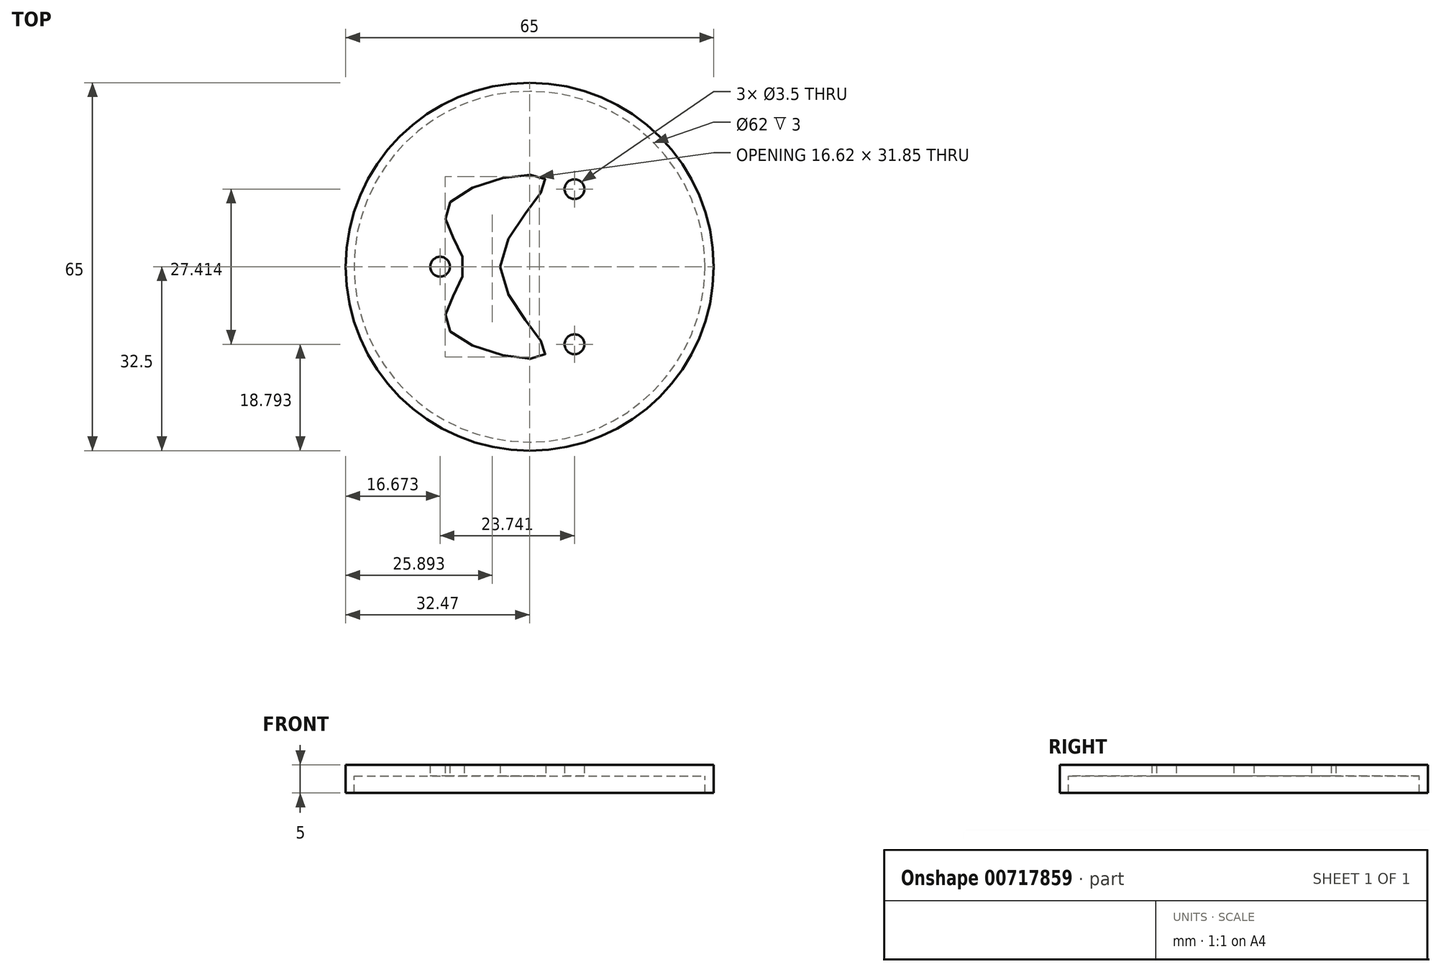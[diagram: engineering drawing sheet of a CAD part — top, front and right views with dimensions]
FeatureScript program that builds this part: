
annotation { "Feature Type Name" : "Feature", "Feature Type Description" : "" }
export const myFeature = defineFeature(function(context is Context, id is Id, definition is map)
    precondition{}
    {
        {
            var Q0;
            Q0=qCreatedBy(makeId("Top.planeOp"),FACE);
            var sketch = newSketch(context, id + "F0", { "sketchPlane" : qUnion([Q0])});
            skCircle(sketch, "E0", {"center": v(0.03, 0) * mm, "radius": 32.5 * mm});
            skCircle(sketch, "E1", {"center": v(-15.8, 0) * mm, "radius": 1.75 * mm});
            skCircle(sketch, "E2.1.0", {"center": v(7.94, -13.7) * mm, "radius": 1.75 * mm});
            skCircle(sketch, "E2.2.0", {"center": v(7.94, 13.7) * mm, "radius": 1.75 * mm});
            skPoint(sketch, "E3", {"position": v(2.67, 15.6) * mm});
            skPoint(sketch, "E4.MirrorP", {"position": v(2.67, -15.6) * mm});
            skPoint(sketch, "E5", {"position": v(-5.16, 0) * mm});
            skPoint(sketch, "E6", {"position": v(-11.57, 0) * mm});
            skPoint(sketch, "E7", {"position": v(-14.47, 10.8) * mm});
            skPoint(sketch, "E8.MirrorP", {"position": v(-14.47, -10.8) * mm});
            skFitSpline(sketch, "E9", {"points": [v(-5.16, 0) * mm, v(2.67, 15.6) * mm, v(-14.47, 10.8) * mm, v(-11.57, 0) * mm, v(-14.47, -10.8) * mm, v(2.67, -15.6) * mm, v(-5.16, 0) * mm]});
            skSolve(sketch);
        }
        {
            var Q0;
            Q0=makeQuery(id+"F0.imprint","IMPRINT",FACE,{"disambiguationData":[TD([[makeQuery(id+"F0.imprint","IMPRINT",EDGE,{"derivedFrom":sQuery(id+"F0.wireOp",EDGE,"E0")}),1.0]])]});
            extrude(context, id + "F1", {"entities" : qUnion([Q0]), "depth" : 2 * mm, "offsetDistance" : 25 * mm});
        }
        {
            var Q0;
            Q0=makeQuery(id+"F1.opExtrude","CAP_FACE",FACE,{"disambiguationData":[OSD([sQuery(id+"F0.wireOp",EDGE,"E0"),sQuery(id+"F0.wireOp",EDGE,"E1"),sQuery(id+"F0.wireOp",EDGE,"E2.1.0"),sQuery(id+"F0.wireOp",EDGE,"E2.2.0"),sQuery(id+"F0.wireOp",EDGE,"E9")])],"isStart":true});
            var sketch = newSketch(context, id + "F2", { "sketchPlane" : qUnion([Q0])});
            skCircle(sketch, "E10", {"center": v(0, 0) * mm, "radius": 31 * mm});
            skSolve(sketch);
        }
        {
            var Q0;
            Q0=makeQuery(id+"F2.imprint","IMPRINT",FACE,{"disambiguationData":[TD([[makeQuery(id+"F2.imprint","IMPRINT",EDGE,{"derivedFrom":sQuery(id+"F2.wireOp",EDGE,"E10")}),-1.0]])]});
            extrude(context, id + "F3", {"entities" : qUnion([Q0]), "operationType" : NewBodyOperationType.ADD, "depth" : 3 * mm, "offsetDistance" : 25 * mm});
        }
    });
